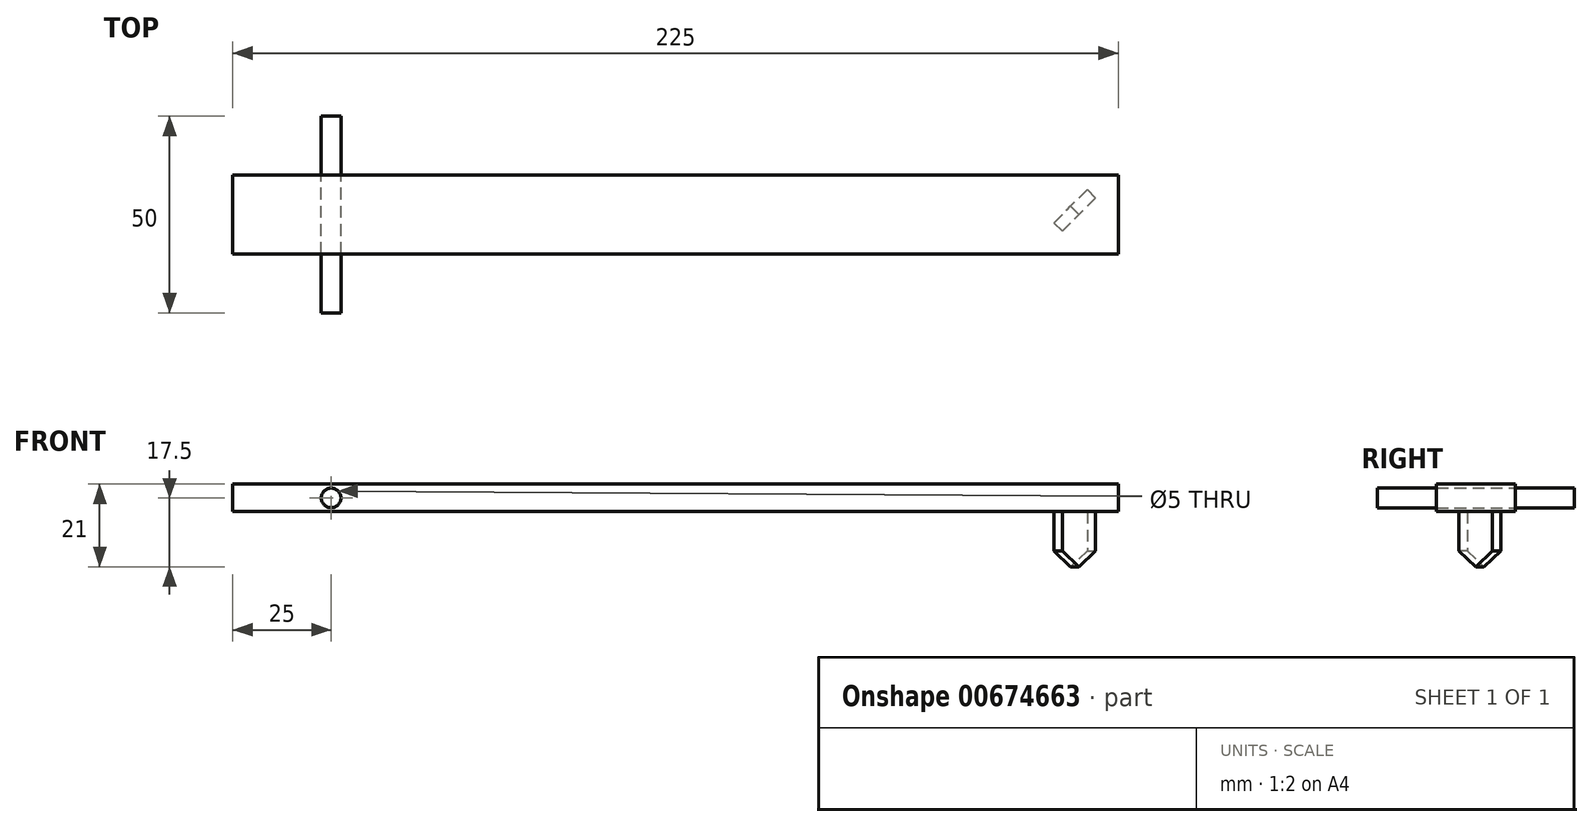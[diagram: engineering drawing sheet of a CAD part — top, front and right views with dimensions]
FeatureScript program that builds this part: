
annotation { "Feature Type Name" : "Feature", "Feature Type Description" : "" }
export const myFeature = defineFeature(function(context is Context, id is Id, definition is map)
    precondition{}
    {
        {
            var Q0;
            Q0=qCreatedBy(makeId("Right.planeOp"),FACE);
            var sketch = newSketch(context, id + "F0", { "sketchPlane" : qUnion([Q0])});
            skLineSegment(sketch, "E0.bottom", {"start": v(-10, 3.5) * mm, "end": v(10, 3.5) * mm});
            skLineSegment(sketch, "E0.top", {"start": v(-10, -3.5) * mm, "end": v(10, -3.5) * mm});
            skLineSegment(sketch, "E0.left", {"start": v(-10, 3.5) * mm, "end": v(-10, -3.5) * mm});
            skLineSegment(sketch, "E0.right", {"start": v(10, 3.5) * mm, "end": v(10, -3.5) * mm});
            skPoint(sketch, "E0.middle", {"position": v(0, 0) * mm});
            skSolve(sketch);
        }
        {
            var Q0;
            Q0=makeQuery(id+"F0.imprint","IMPRINT",FACE,{"disambiguationData":[TD([[makeQuery(id+"F0.imprint","IMPRINT",EDGE,{"derivedFrom":sQuery(id+"F0.wireOp",EDGE,"E0.bottom")}),-1.0]])]});
            extrude(context, id + "F1", {"entities" : qUnion([Q0]), "depth" : 200 * mm, "offsetDistance" : 25 * mm});
        }
        {
            var Q0;
            Q0=makeQuery(id+"F1.opExtrude","CAP_FACE",FACE,{"disambiguationData":[OSD([sQuery(id+"F0.wireOp",EDGE,"E0.bottom"),sQuery(id+"F0.wireOp",EDGE,"E0.top"),sQuery(id+"F0.wireOp",EDGE,"E0.left"),sQuery(id+"F0.wireOp",EDGE,"E0.right")])],"isStart":true});
            extrude(context, id + "F2", {"entities" : qUnion([Q0]), "operationType" : NewBodyOperationType.ADD, "depth" : 25 * mm, "offsetDistance" : 25 * mm});
        }
        {
            var Q0;
            {var subQ0=sQuery(id+"F0.wireOp",EDGE,"E0.left");Q0=makeQuery(id+"F2.boolean.opBoolean","MERGE",FACE,{"derivedFrom":[makeQuery(id+"F1.opExtrude","SWEPT_FACE",FACE,{"disambiguationData":[OSD([subQ0])]}),makeQuery(id+"F2.opExtrude","SWEPT_FACE",FACE,{"disambiguationData":[OSD([subQ0])]})]});}
            var sketch = newSketch(context, id + "F3", { "sketchPlane" : qUnion([Q0])});
            skCircle(sketch, "E1", {"center": v(0, 0) * mm, "radius": 2.5 * mm});
            skSolve(sketch);
        }
        {
            var Q0;
            Q0=makeQuery(id+"F3.imprint","IMPRINT",FACE,{"disambiguationData":[TD([[makeQuery(id+"F3.imprint","IMPRINT",EDGE,{"derivedFrom":sQuery(id+"F3.wireOp",EDGE,"E1")}),1.0]])]});
            extrude(context, id + "F4", {"entities" : qUnion([Q0]), "operationType" : NewBodyOperationType.REMOVE, "endBound" : BoundingType.UP_TO_NEXT, "oppositeDirection" : true, "depth" : 25 * mm, "offsetDistance" : 25 * mm});
        }
        {
            var Q0;
            Q0=qCreatedBy(makeId("Front.planeOp"),FACE);
            var sketch = newSketch(context, id + "F5", { "sketchPlane" : qUnion([Q0])});
            skCircle(sketch, "E2.0", {"center": v(0, 0) * mm, "radius": 2.5 * mm});
            skSolve(sketch);
        }
        {
            var Q0;
            Q0 = qSketchRegion(id + "F5", true);
            var Q1;
            Q1=sQuery(id+"F5.wireOp",EDGE,"E2.0");
            extrude(context, id + "F6", {"entities" : qUnion([Q0]), "surfaceEntities" : qUnion([Q1]), "endBound" : BoundingType.SYMMETRIC, "depth" : 50 * mm, "offsetDistance" : 25 * mm});
        }
        {
            var Q0;
            {var subQ0=sQuery(id+"F0.wireOp",EDGE,"E0.bottom");Q0=makeQuery(id+"F2.boolean.opBoolean","MERGE",FACE,{"derivedFrom":[makeQuery(id+"F1.opExtrude","SWEPT_FACE",FACE,{"disambiguationData":[OSD([subQ0])]}),makeQuery(id+"F2.opExtrude","SWEPT_FACE",FACE,{"disambiguationData":[OSD([subQ0])]})]});}
            var sketch = newSketch(context, id + "F7", { "sketchPlane" : qUnion([Q0])});
            skPoint(sketch, "E3.0", {"position": v(200, 0) * mm});
            skLineSegment(sketch, "E4.0", {"start": v(200, 10) * mm, "end": v(-25, 10) * mm});
            skLineSegment(sketch, "E5.0", {"start": v(200, -10) * mm, "end": v(-25, -10) * mm});
            skLineSegment(sketch, "E6.0", {"start": v(200, -10) * mm, "end": v(200, 10) * mm});
            skLineSegment(sketch, "E7", {"start": v(171.23, -18.77) * mm, "end": v(213.39, 23.39) * mm, "construction": true});
            skLineSegment(sketch, "E8", {"start": v(200, 0) * mm, "end": v(165.06, 0) * mm, "construction": true});
            skPoint(sketch, "E9", {"position": v(190, 0) * mm});
            skSolve(sketch);
        }
        {
            var Q0;
            Q0=sQuery(id+"F7.wireOp",EDGE,"E7");
            var Q1;
            Q1=makeQuery(id+"F1.opExtrude","CAP_FACE",FACE,{"disambiguationData":[OSD([sQuery(id+"F0.wireOp",EDGE,"E0.bottom"),sQuery(id+"F0.wireOp",EDGE,"E0.top"),sQuery(id+"F0.wireOp",EDGE,"E0.left"),sQuery(id+"F0.wireOp",EDGE,"E0.right")])],"isStart":false});
            cPlane(context, id + "F8", {"entities" : qUnion([Q0, Q1]), "cplaneType" : CPlaneType.LINE_ANGLE, "offset" : 25 * mm, "angle" : 0 * degree, "width" : 150 * mm, "height" : 150 * mm});
        }
        {
            var Q0;
            Q0=qCreatedBy(id+"F8.planeOp",FACE);
            var sketch = newSketch(context, id + "F9", { "sketchPlane" : qUnion([Q0])});
            skLineSegment(sketch, "E10.0", {"start": v(-148.5, -3.5) * mm, "end": v(10.6, -3.5) * mm});
            skPoint(sketch, "E11.0", {"position": v(-134.35, 3.5) * mm});
            skLineSegment(sketch, "E12", {"start": v(-134.35, 3.5) * mm, "end": v(-134.35, -41.16) * mm, "construction": true});
            skLineSegment(sketch, "E13", {"start": v(-128.35, -3.5) * mm, "end": v(-128.35, -13.5) * mm});
            skLineSegment(sketch, "E14", {"start": v(-128.35, -13.5) * mm, "end": v(-134.35, -17.5) * mm});
            skLineSegment(sketch, "E15.MirrorCS", {"start": v(-140.35, -3.5) * mm, "end": v(-140.35, -13.5) * mm});
            skLineSegment(sketch, "E16.MirrorCS", {"start": v(-140.35, -13.5) * mm, "end": v(-134.35, -17.5) * mm});
            skSolve(sketch);
        }
        {
            var Q0;
            {var subQ1=sQuery(id+"F9.wireOp",EDGE,"E13");Q0=makeQuery(id+"F9.imprint","IMPRINT",FACE,{"disambiguationData":[TD([[makeQuery(id+"F9.imprint","IMPRINT",EDGE,{"derivedFrom":subQ1}),-1.0]])]});}
            extrude(context, id + "F10", {"entities" : qUnion([Q0]), "depth" : 3 * mm, "offsetDistance" : 25 * mm});
        }
    });
